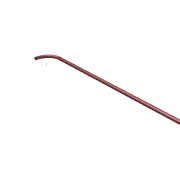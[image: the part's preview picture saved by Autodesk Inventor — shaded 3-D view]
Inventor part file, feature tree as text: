
AUTODESK INVENTOR PART (.ipt)
format: ipt  version: unknown  size: 162,816 bytes
history: native  units: mm
features: sketch x2, sweep x1, split x1
ambient origin geometry x8: Origin, YZ Plane, XZ Plane, XY Plane, X Axis, Y Axis, Z Axis, Center Point
feature tree (4):
  sweep  "Sweep1"
  split  "Split1"
  sketch  "Sketch1"  dims[d0=80.0mm d1=20.0mm]
  sketch  "Sketch2"  dims[d2=10.0mm d3=2.0mm d4=0.0mm d5=80.0mm]
